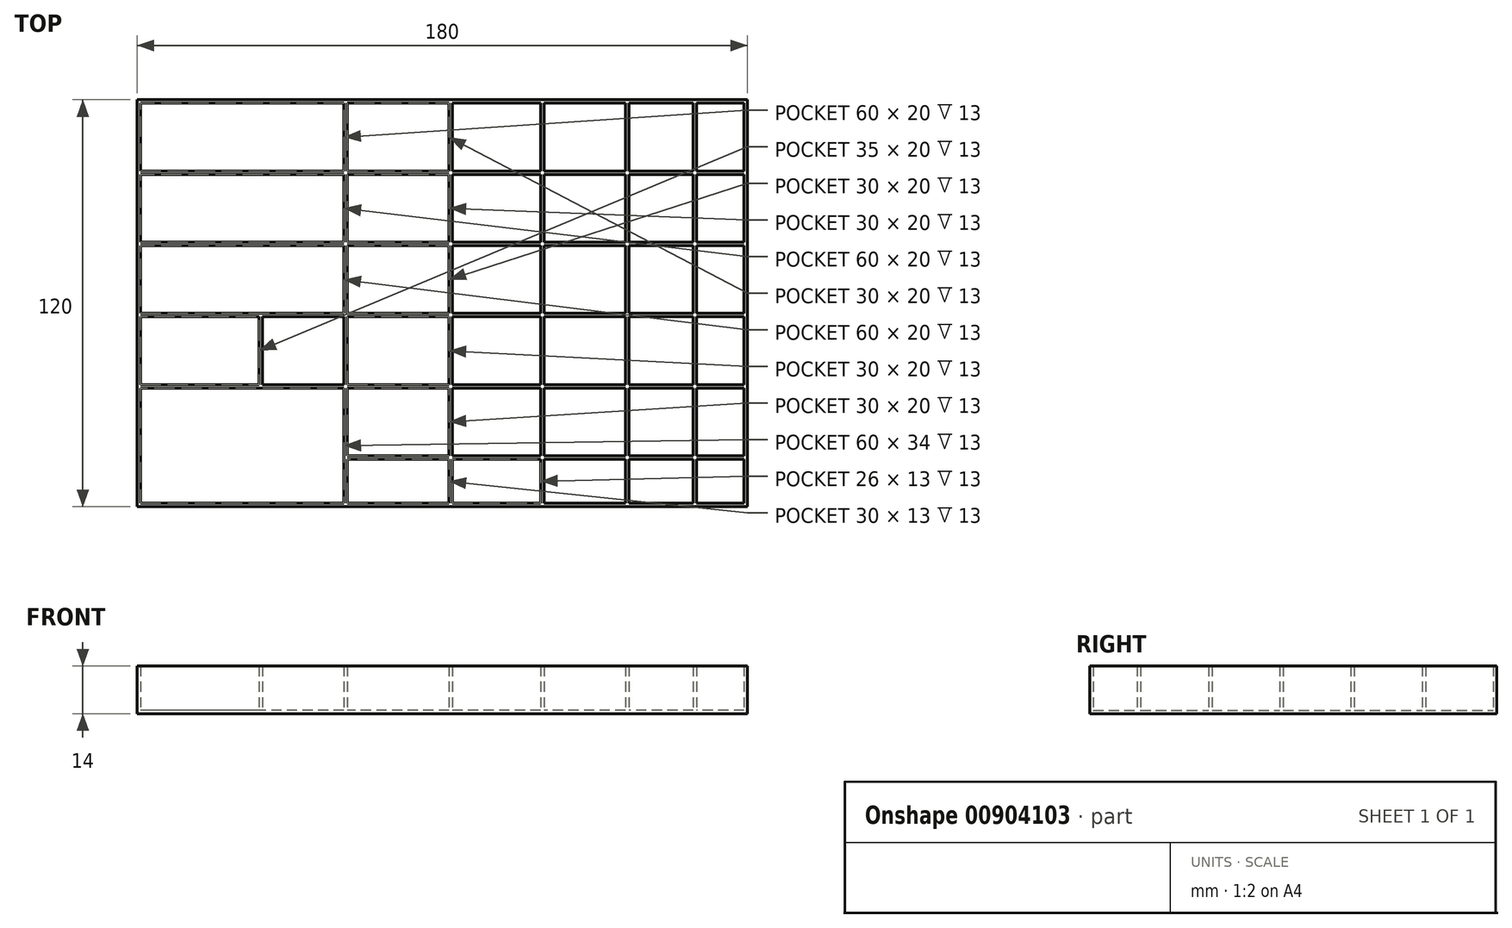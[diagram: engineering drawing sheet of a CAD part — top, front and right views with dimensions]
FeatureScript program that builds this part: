
annotation { "Feature Type Name" : "Feature", "Feature Type Description" : "" }
export const myFeature = defineFeature(function(context is Context, id is Id, definition is map)
    precondition{}
    {
        {
            var Q0;
            Q0=qCreatedBy(makeId("Top.planeOp"),FACE);
            var sketch = newSketch(context, id + "F0", { "sketchPlane" : qUnion([Q0])});
            skPoint(sketch, "E0.0", {"position": v(-113.76, 55.2) * mm});
            skPoint(sketch, "E0.1", {"position": v(66.24, -64.8) * mm});
            skLineSegment(sketch, "E1.bottom", {"start": v(-113.76, 55.2) * mm, "end": v(66.24, 55.2) * mm});
            skLineSegment(sketch, "E1.top", {"start": v(-113.76, -64.8) * mm, "end": v(66.24, -64.8) * mm});
            skLineSegment(sketch, "E1.left", {"start": v(-113.76, 55.2) * mm, "end": v(-113.76, -64.8) * mm});
            skLineSegment(sketch, "E1.right", {"start": v(66.24, 55.2) * mm, "end": v(66.24, -64.8) * mm});
            skSolve(sketch);
        }
        {
            var Q0;
            Q0 = qSketchRegion(id + "F0", true);
            extrude(context, id + "F1", {"entities" : qUnion([Q0]), "depth" : 1 * mm, "offsetDistance" : 25 * mm});
        }
        {
            var Q0;
            Q0=qCreatedBy(makeId("Top.planeOp"),FACE);
            var sketch = newSketch(context, id + "F2", { "sketchPlane" : qUnion([Q0])});
            skLineSegment(sketch, "E2.bottom", {"start": v(-113.76, 55.2) * mm, "end": v(66.24, 55.2) * mm});
            skLineSegment(sketch, "E2.top", {"start": v(-113.76, -64.8) * mm, "end": v(66.24, -64.8) * mm});
            skLineSegment(sketch, "E2.left", {"start": v(-113.76, 55.2) * mm, "end": v(-113.76, -64.8) * mm});
            skLineSegment(sketch, "E2.right", {"start": v(66.24, 55.2) * mm, "end": v(66.24, -64.8) * mm});
            skLineSegment(sketch, "E3.0", {"start": v(-112.76, 54.2) * mm, "end": v(-52.76, 54.2) * mm});
            skLineSegment(sketch, "E3.1", {"start": v(-112.76, 54.2) * mm, "end": v(-112.76, 34.2) * mm});
            skLineSegment(sketch, "E3.2", {"start": v(-112.76, -63.8) * mm, "end": v(-52.76, -63.8) * mm});
            skLineSegment(sketch, "E3.3", {"start": v(65.24, 54.2) * mm, "end": v(65.24, 34.2) * mm});
            skLineSegment(sketch, "E4", {"start": v(-112.76, 34.2) * mm, "end": v(-52.76, 34.2) * mm});
            skLineSegment(sketch, "E5", {"start": v(-112.76, 13.2) * mm, "end": v(-52.76, 13.2) * mm});
            skLineSegment(sketch, "E6", {"start": v(-112.76, -7.8) * mm, "end": v(-52.76, -7.8) * mm});
            skLineSegment(sketch, "E7", {"start": v(-112.76, -28.8) * mm, "end": v(-77.76, -28.8) * mm});
            skLineSegment(sketch, "E8", {"start": v(-52.76, 54.2) * mm, "end": v(-52.76, 34.2) * mm});
            skLineSegment(sketch, "E9", {"start": v(-21.76, 54.2) * mm, "end": v(-21.76, 34.2) * mm});
            skLineSegment(sketch, "E10", {"start": v(5.24, 54.2) * mm, "end": v(5.24, 34.2) * mm});
            skLineSegment(sketch, "E11", {"start": v(30.24, 54.2) * mm, "end": v(30.24, 34.2) * mm});
            skLineSegment(sketch, "E12", {"start": v(50.24, 54.2) * mm, "end": v(50.24, 34.2) * mm});
            skLineSegment(sketch, "E13.0", {"start": v(-51.76, 54.2) * mm, "end": v(-51.76, 34.2) * mm});
            skLineSegment(sketch, "E14.0", {"start": v(-20.76, 54.2) * mm, "end": v(-20.76, 34.2) * mm});
            skLineSegment(sketch, "E15.0", {"start": v(6.24, 54.2) * mm, "end": v(6.24, 34.2) * mm});
            skLineSegment(sketch, "E16.0", {"start": v(31.24, 54.2) * mm, "end": v(31.24, 34.2) * mm});
            skLineSegment(sketch, "E17.0", {"start": v(51.24, 54.2) * mm, "end": v(51.24, 34.2) * mm});
            skLineSegment(sketch, "E18.0", {"start": v(-51.76, 33.2) * mm, "end": v(-21.76, 33.2) * mm});
            skLineSegment(sketch, "E19.0", {"start": v(-112.76, 12.2) * mm, "end": v(-52.76, 12.2) * mm});
            skLineSegment(sketch, "E20.0", {"start": v(-112.76, -8.8) * mm, "end": v(-77.76, -8.8) * mm});
            skLineSegment(sketch, "E21", {"start": v(-77.76, -8.8) * mm, "end": v(-77.76, -28.8) * mm});
            skLineSegment(sketch, "E22.0", {"start": v(-76.76, -8.8) * mm, "end": v(-76.76, -28.8) * mm});
            skLineSegment(sketch, "E23.trimOffspring", {"start": v(-112.76, 33.2) * mm, "end": v(-112.76, 13.2) * mm});
            skLineSegment(sketch, "E24.trimOffspring", {"start": v(-112.76, 12.2) * mm, "end": v(-112.76, -7.8) * mm});
            skLineSegment(sketch, "E25.trimOffspring", {"start": v(-112.76, -8.8) * mm, "end": v(-112.76, -28.8) * mm});
            skLineSegment(sketch, "E26.trimOffspring", {"start": v(-76.76, -8.8) * mm, "end": v(-52.76, -8.8) * mm});
            skLineSegment(sketch, "E27.trimOffspring", {"start": v(-76.76, -28.8) * mm, "end": v(-52.76, -28.8) * mm});
            skLineSegment(sketch, "E28.trimOffspring", {"start": v(-112.76, -29.8) * mm, "end": v(-52.76, -29.8) * mm});
            skLineSegment(sketch, "E29.trimOffspring", {"start": v(-112.76, -29.8) * mm, "end": v(-112.76, -63.8) * mm});
            skLineSegment(sketch, "E30.trimOffspring", {"start": v(-51.76, -63.8) * mm, "end": v(-21.76, -63.8) * mm});
            skLineSegment(sketch, "E31.trimOffspring", {"start": v(-51.76, -49.8) * mm, "end": v(-21.76, -49.8) * mm});
            skLineSegment(sketch, "E32.trimOffspring", {"start": v(-51.76, -50.8) * mm, "end": v(-51.76, -63.8) * mm});
            skLineSegment(sketch, "E33.trimOffspring", {"start": v(-51.76, -50.8) * mm, "end": v(-21.76, -50.8) * mm});
            skLineSegment(sketch, "E34.trimOffspring", {"start": v(-20.76, -63.8) * mm, "end": v(5.24, -63.8) * mm});
            skLineSegment(sketch, "E35.trimOffspring", {"start": v(-21.76, -50.8) * mm, "end": v(-21.76, -63.8) * mm});
            skLineSegment(sketch, "E36.trimOffspring", {"start": v(-20.76, -50.8) * mm, "end": v(-20.76, -63.8) * mm});
            skLineSegment(sketch, "E37.trimOffspring", {"start": v(-20.76, -49.8) * mm, "end": v(5.24, -49.8) * mm});
            skLineSegment(sketch, "E38.trimOffspring", {"start": v(-20.76, -50.8) * mm, "end": v(5.24, -50.8) * mm});
            skLineSegment(sketch, "E39.trimOffspring", {"start": v(6.24, -63.8) * mm, "end": v(30.24, -63.8) * mm});
            skLineSegment(sketch, "E40.trimOffspring", {"start": v(5.24, -50.8) * mm, "end": v(5.24, -63.8) * mm});
            skLineSegment(sketch, "E41.trimOffspring", {"start": v(6.24, -49.8) * mm, "end": v(30.24, -49.8) * mm});
            skLineSegment(sketch, "E42.trimOffspring", {"start": v(6.24, -50.8) * mm, "end": v(6.24, -63.8) * mm});
            skLineSegment(sketch, "E43.trimOffspring", {"start": v(6.24, -50.8) * mm, "end": v(30.24, -50.8) * mm});
            skLineSegment(sketch, "E44.trimOffspring", {"start": v(31.24, -49.8) * mm, "end": v(50.24, -49.8) * mm});
            skLineSegment(sketch, "E45.trimOffspring", {"start": v(30.24, -50.8) * mm, "end": v(30.24, -63.8) * mm});
            skLineSegment(sketch, "E46.trimOffspring", {"start": v(31.24, -50.8) * mm, "end": v(50.24, -50.8) * mm});
            skLineSegment(sketch, "E47.trimOffspring", {"start": v(31.24, -50.8) * mm, "end": v(31.24, -63.8) * mm});
            skLineSegment(sketch, "E48.trimOffspring", {"start": v(31.24, -63.8) * mm, "end": v(50.24, -63.8) * mm});
            skLineSegment(sketch, "E49.trimOffspring", {"start": v(51.24, -63.8) * mm, "end": v(65.24, -63.8) * mm});
            skLineSegment(sketch, "E50.trimOffspring", {"start": v(51.24, -50.8) * mm, "end": v(65.24, -50.8) * mm});
            skLineSegment(sketch, "E51.trimOffspring", {"start": v(50.24, -50.8) * mm, "end": v(50.24, -63.8) * mm});
            skLineSegment(sketch, "E52.trimOffspring", {"start": v(51.24, -49.8) * mm, "end": v(65.24, -49.8) * mm});
            skLineSegment(sketch, "E53.trimOffspring", {"start": v(51.24, -50.8) * mm, "end": v(51.24, -63.8) * mm});
            skLineSegment(sketch, "E54.trimOffspring", {"start": v(65.24, -50.8) * mm, "end": v(65.24, -63.8) * mm});
            skLineSegment(sketch, "E55.trimOffspring", {"start": v(-52.76, -29.8) * mm, "end": v(-52.76, -63.8) * mm});
            skLineSegment(sketch, "E56.trimOffspring", {"start": v(-51.76, -28.8) * mm, "end": v(-21.76, -28.8) * mm});
            skLineSegment(sketch, "E57.trimOffspring", {"start": v(-51.76, -29.8) * mm, "end": v(-51.76, -49.8) * mm});
            skLineSegment(sketch, "E58.trimOffspring", {"start": v(-51.76, -29.8) * mm, "end": v(-21.76, -29.8) * mm});
            skLineSegment(sketch, "E59.trimOffspring", {"start": v(-21.76, -29.8) * mm, "end": v(-21.76, -49.8) * mm});
            skLineSegment(sketch, "E60.trimOffspring", {"start": v(-20.76, -28.8) * mm, "end": v(5.24, -28.8) * mm});
            skLineSegment(sketch, "E61.trimOffspring", {"start": v(-20.76, -29.8) * mm, "end": v(-20.76, -49.8) * mm});
            skLineSegment(sketch, "E62.trimOffspring", {"start": v(-20.76, -29.8) * mm, "end": v(5.24, -29.8) * mm});
            skLineSegment(sketch, "E63.trimOffspring", {"start": v(5.24, -29.8) * mm, "end": v(5.24, -49.8) * mm});
            skLineSegment(sketch, "E64.trimOffspring", {"start": v(6.24, -28.8) * mm, "end": v(30.24, -28.8) * mm});
            skLineSegment(sketch, "E65.trimOffspring", {"start": v(6.24, -29.8) * mm, "end": v(6.24, -49.8) * mm});
            skLineSegment(sketch, "E66.trimOffspring", {"start": v(6.24, -29.8) * mm, "end": v(30.24, -29.8) * mm});
            skLineSegment(sketch, "E67.trimOffspring", {"start": v(51.24, -29.8) * mm, "end": v(51.24, -49.8) * mm});
            skLineSegment(sketch, "E68.trimOffspring", {"start": v(51.24, -28.8) * mm, "end": v(65.24, -28.8) * mm});
            skLineSegment(sketch, "E69.trimOffspring", {"start": v(51.24, -29.8) * mm, "end": v(65.24, -29.8) * mm});
            skLineSegment(sketch, "E70.trimOffspring", {"start": v(50.24, -29.8) * mm, "end": v(50.24, -49.8) * mm});
            skLineSegment(sketch, "E71.trimOffspring", {"start": v(31.24, -29.8) * mm, "end": v(31.24, -49.8) * mm});
            skLineSegment(sketch, "E72.trimOffspring", {"start": v(31.24, -28.8) * mm, "end": v(50.24, -28.8) * mm});
            skLineSegment(sketch, "E73.trimOffspring", {"start": v(30.24, -29.8) * mm, "end": v(30.24, -49.8) * mm});
            skLineSegment(sketch, "E74.trimOffspring", {"start": v(31.24, -29.8) * mm, "end": v(50.24, -29.8) * mm});
            skLineSegment(sketch, "E75.trimOffspring", {"start": v(65.24, -29.8) * mm, "end": v(65.24, -49.8) * mm});
            skLineSegment(sketch, "E76.trimOffspring", {"start": v(65.24, 12.2) * mm, "end": v(65.24, -7.8) * mm});
            skLineSegment(sketch, "E77.trimOffspring", {"start": v(65.24, -8.8) * mm, "end": v(65.24, -28.8) * mm});
            skLineSegment(sketch, "E78.trimOffspring", {"start": v(51.24, -8.8) * mm, "end": v(51.24, -28.8) * mm});
            skLineSegment(sketch, "E79.trimOffspring", {"start": v(51.24, -7.8) * mm, "end": v(65.24, -7.8) * mm});
            skLineSegment(sketch, "E80.trimOffspring", {"start": v(50.24, -8.8) * mm, "end": v(50.24, -28.8) * mm});
            skLineSegment(sketch, "E81.trimOffspring", {"start": v(51.24, -8.8) * mm, "end": v(65.24, -8.8) * mm});
            skLineSegment(sketch, "E82.trimOffspring", {"start": v(31.24, -8.8) * mm, "end": v(31.24, -28.8) * mm});
            skLineSegment(sketch, "E83.trimOffspring", {"start": v(31.24, -7.8) * mm, "end": v(50.24, -7.8) * mm});
            skLineSegment(sketch, "E84.trimOffspring", {"start": v(30.24, -8.8) * mm, "end": v(30.24, -28.8) * mm});
            skLineSegment(sketch, "E85.trimOffspring", {"start": v(31.24, -8.8) * mm, "end": v(50.24, -8.8) * mm});
            skLineSegment(sketch, "E86.trimOffspring", {"start": v(51.24, 12.2) * mm, "end": v(51.24, -7.8) * mm});
            skLineSegment(sketch, "E87.trimOffspring", {"start": v(51.24, 13.2) * mm, "end": v(65.24, 13.2) * mm});
            skLineSegment(sketch, "E88.trimOffspring", {"start": v(50.24, 12.2) * mm, "end": v(50.24, -7.8) * mm});
            skLineSegment(sketch, "E89.trimOffspring", {"start": v(51.24, 12.2) * mm, "end": v(65.24, 12.2) * mm});
            skLineSegment(sketch, "E90.trimOffspring", {"start": v(6.24, -8.8) * mm, "end": v(6.24, -28.8) * mm});
            skLineSegment(sketch, "E91.trimOffspring", {"start": v(5.24, -8.8) * mm, "end": v(5.24, -28.8) * mm});
            skLineSegment(sketch, "E92.trimOffspring", {"start": v(6.24, -8.8) * mm, "end": v(30.24, -8.8) * mm});
            skLineSegment(sketch, "E93.trimOffspring", {"start": v(6.24, -7.8) * mm, "end": v(30.24, -7.8) * mm});
            skLineSegment(sketch, "E94.trimOffspring", {"start": v(6.24, 12.2) * mm, "end": v(6.24, -7.8) * mm});
            skLineSegment(sketch, "E95.trimOffspring", {"start": v(6.24, 13.2) * mm, "end": v(30.24, 13.2) * mm});
            skLineSegment(sketch, "E96.trimOffspring", {"start": v(5.24, 12.2) * mm, "end": v(5.24, -7.8) * mm});
            skLineSegment(sketch, "E97.trimOffspring", {"start": v(6.24, 12.2) * mm, "end": v(30.24, 12.2) * mm});
            skLineSegment(sketch, "E98.trimOffspring", {"start": v(-20.76, 13.2) * mm, "end": v(5.24, 13.2) * mm});
            skLineSegment(sketch, "E99.trimOffspring", {"start": v(-21.76, 12.2) * mm, "end": v(-21.76, -7.8) * mm});
            skLineSegment(sketch, "E100.trimOffspring", {"start": v(-20.76, 12.2) * mm, "end": v(-20.76, -7.8) * mm});
            skLineSegment(sketch, "E101.trimOffspring", {"start": v(-20.76, 12.2) * mm, "end": v(5.24, 12.2) * mm});
            skLineSegment(sketch, "E102.trimOffspring", {"start": v(-20.76, -8.8) * mm, "end": v(-20.76, -28.8) * mm});
            skLineSegment(sketch, "E103.trimOffspring", {"start": v(-20.76, -7.8) * mm, "end": v(5.24, -7.8) * mm});
            skLineSegment(sketch, "E104.trimOffspring", {"start": v(-21.76, -8.8) * mm, "end": v(-21.76, -28.8) * mm});
            skLineSegment(sketch, "E105.trimOffspring", {"start": v(-20.76, -8.8) * mm, "end": v(5.24, -8.8) * mm});
            skLineSegment(sketch, "E106.trimOffspring", {"start": v(-51.76, -8.8) * mm, "end": v(-51.76, -28.8) * mm});
            skLineSegment(sketch, "E107.trimOffspring", {"start": v(-51.76, -7.8) * mm, "end": v(-21.76, -7.8) * mm});
            skLineSegment(sketch, "E108.trimOffspring", {"start": v(-52.76, -8.8) * mm, "end": v(-52.76, -28.8) * mm});
            skLineSegment(sketch, "E109.trimOffspring", {"start": v(-51.76, -8.8) * mm, "end": v(-21.76, -8.8) * mm});
            skLineSegment(sketch, "E110.trimOffspring", {"start": v(-51.76, 12.2) * mm, "end": v(-51.76, -7.8) * mm});
            skLineSegment(sketch, "E111.trimOffspring", {"start": v(-52.76, 12.2) * mm, "end": v(-52.76, -7.8) * mm});
            skLineSegment(sketch, "E112.trimOffspring", {"start": v(-51.76, 12.2) * mm, "end": v(-21.76, 12.2) * mm});
            skLineSegment(sketch, "E113.trimOffspring", {"start": v(-51.76, 34.2) * mm, "end": v(-21.76, 34.2) * mm});
            skLineSegment(sketch, "E114.trimOffspring", {"start": v(-51.76, 33.2) * mm, "end": v(-51.76, 13.2) * mm});
            skLineSegment(sketch, "E115.trimOffspring", {"start": v(-51.76, 54.2) * mm, "end": v(-21.76, 54.2) * mm});
            skLineSegment(sketch, "E116.trimOffspring", {"start": v(-20.76, 54.2) * mm, "end": v(5.24, 54.2) * mm});
            skLineSegment(sketch, "E117", {"start": v(-52.76, 33.2) * mm, "end": v(-52.76, 13.2) * mm});
            skLineSegment(sketch, "E118.trimOffspring", {"start": v(-20.76, 34.2) * mm, "end": v(5.24, 34.2) * mm});
            skLineSegment(sketch, "E119.trimOffspring", {"start": v(-21.76, 33.2) * mm, "end": v(-21.76, 13.2) * mm});
            skLineSegment(sketch, "E120.trimOffspring", {"start": v(-20.76, 33.2) * mm, "end": v(-20.76, 13.2) * mm});
            skLineSegment(sketch, "E121.trimOffspring", {"start": v(-20.76, 33.2) * mm, "end": v(5.24, 33.2) * mm});
            skLineSegment(sketch, "E122.trimOffspring", {"start": v(6.24, 54.2) * mm, "end": v(30.24, 54.2) * mm});
            skLineSegment(sketch, "E123.trimOffspring", {"start": v(6.24, 34.2) * mm, "end": v(30.24, 34.2) * mm});
            skLineSegment(sketch, "E124.trimOffspring", {"start": v(5.24, 33.2) * mm, "end": v(5.24, 13.2) * mm});
            skLineSegment(sketch, "E125.trimOffspring", {"start": v(6.24, 33.2) * mm, "end": v(30.24, 33.2) * mm});
            skLineSegment(sketch, "E126.trimOffspring", {"start": v(6.24, 33.2) * mm, "end": v(6.24, 13.2) * mm});
            skLineSegment(sketch, "E127.trimOffspring", {"start": v(31.24, 54.2) * mm, "end": v(50.24, 54.2) * mm});
            skLineSegment(sketch, "E128.trimOffspring", {"start": v(31.24, 34.2) * mm, "end": v(50.24, 34.2) * mm});
            skLineSegment(sketch, "E129.trimOffspring", {"start": v(30.24, 33.2) * mm, "end": v(30.24, 13.2) * mm});
            skLineSegment(sketch, "E130.trimOffspring", {"start": v(31.24, 33.2) * mm, "end": v(50.24, 33.2) * mm});
            skLineSegment(sketch, "E131.trimOffspring", {"start": v(31.24, 33.2) * mm, "end": v(31.24, 13.2) * mm});
            skLineSegment(sketch, "E132.trimOffspring", {"start": v(51.24, 54.2) * mm, "end": v(65.24, 54.2) * mm});
            skLineSegment(sketch, "E133.trimOffspring", {"start": v(65.24, 33.2) * mm, "end": v(65.24, 13.2) * mm});
            skLineSegment(sketch, "E134.trimOffspring", {"start": v(51.24, 34.2) * mm, "end": v(65.24, 34.2) * mm});
            skLineSegment(sketch, "E135.trimOffspring", {"start": v(50.24, 33.2) * mm, "end": v(50.24, 13.2) * mm});
            skLineSegment(sketch, "E136.trimOffspring", {"start": v(51.24, 33.2) * mm, "end": v(51.24, 13.2) * mm});
            skLineSegment(sketch, "E137.trimOffspring", {"start": v(51.24, 33.2) * mm, "end": v(65.24, 33.2) * mm});
            skLineSegment(sketch, "E138.trimOffspring", {"start": v(31.24, 13.2) * mm, "end": v(50.24, 13.2) * mm});
            skLineSegment(sketch, "E139.trimOffspring", {"start": v(31.24, 12.2) * mm, "end": v(31.24, -7.8) * mm});
            skLineSegment(sketch, "E140.trimOffspring", {"start": v(31.24, 12.2) * mm, "end": v(50.24, 12.2) * mm});
            skLineSegment(sketch, "E141.trimOffspring", {"start": v(30.24, 12.2) * mm, "end": v(30.24, -7.8) * mm});
            skLineSegment(sketch, "E142", {"start": v(-112.76, 33.2) * mm, "end": v(-52.76, 33.2) * mm});
            skLineSegment(sketch, "E143.trimOffspring", {"start": v(-51.76, 13.2) * mm, "end": v(-21.76, 13.2) * mm});
            skSolve(sketch);
        }
        {
            var Q0;
            Q0=makeQuery(id+"F2.imprint","IMPRINT",FACE,{"disambiguationData":[TD([[makeQuery(id+"F2.imprint","IMPRINT",EDGE,{"derivedFrom":sQuery(id+"F2.wireOp",EDGE,"E2.bottom")}),-1.0]])]});
            extrude(context, id + "F3", {"entities" : qUnion([Q0]), "operationType" : NewBodyOperationType.ADD, "depth" : 14 * mm, "offsetDistance" : 25 * mm});
        }
    });
